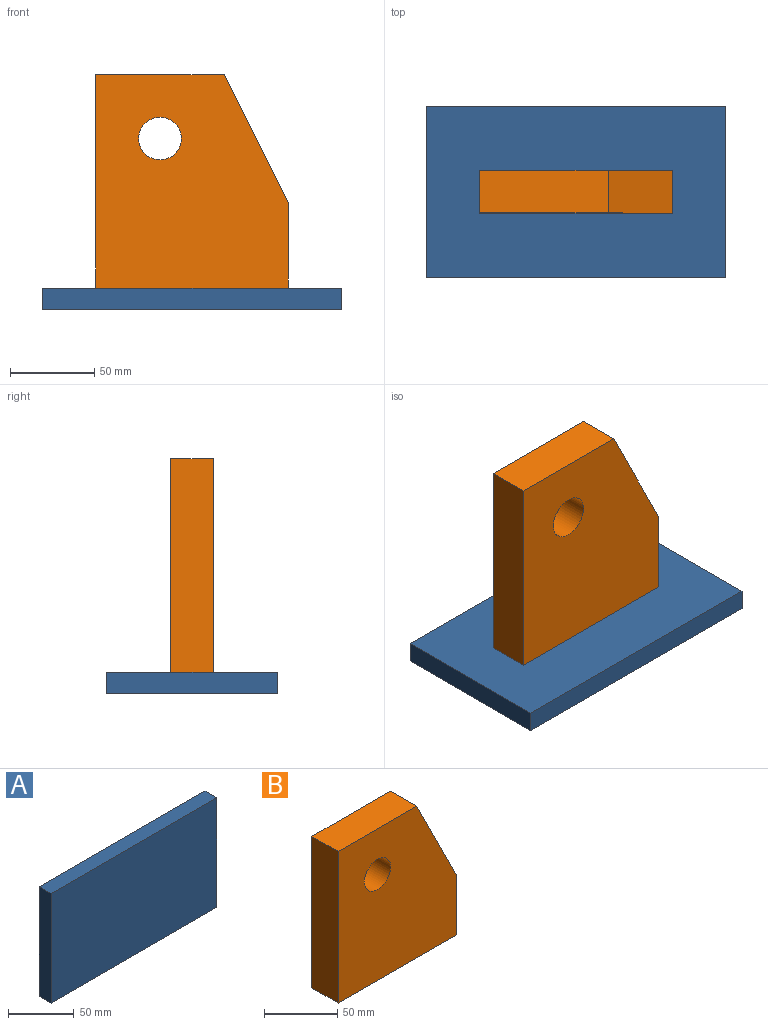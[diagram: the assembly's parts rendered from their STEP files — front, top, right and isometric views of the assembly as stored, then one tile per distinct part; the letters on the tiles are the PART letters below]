
ASSEMBLY  parts=2 mates=1
PART A: 6 faces, bbox 177.8x12.7x101.6 mm
  f0: plane 177.8x12.7mm, normal (0,0,1), area 2258.1mm2, adj f1,f3,f4,f5
  f1: plane 101.6x12.7mm, normal (-1,0,0), area 1290.3mm2, adj f0,f2,f4,f5
  f2: plane 177.8x12.7mm, normal (0,0,-1), area 2258.1mm2, adj f1,f3,f4,f5
  f3: plane 101.6x12.7mm, normal (1,0,0), area 1290.3mm2, adj f0,f2,f4,f5
  f4: plane 177.8x101.6mm, normal (0,-1,0), area 18064.5mm2, adj f0,f1,f2,f3
  f5: plane 177.8x101.6mm, normal (0,1,0), area 18064.5mm2, adj f0,f1,f2,f3
PART B: 8 faces, bbox 114.3x25.4x127 mm
  f0: plane 76.2x25.4mm, normal (0,0,1), area 1935.5mm2, adj f1,f5,f6,f7
  f1: plane 127x25.4mm, normal (-1,0,0), area 3225.8mm2, adj f0,f2,f6,f7
  f2: plane 114.3x25.4mm, normal (0,0,-1), area 2903.2mm2, adj f1,f3,f6,f7
  f3: plane 50.8x25.4mm, normal (1,0,0), area 1290.3mm2, adj f2,f5,f6,f7
  f4: cylinder r=12.7mm len=25.4mm, axis (0,1,0), area 2026.8mm2, adj f6,f7
  f5: plane 76.2x38.1mm, normal (0.89,0,0.45), area 2163.9mm2, adj f0,f3,f6,f7
  f6: plane 127x114.3mm, normal (0,-1,0), area 12557.8mm2, adj f0,f1,f2,f3,f4,f5
  f7: plane 127x114.3mm, normal (0,1,0), area 12557.8mm2, adj f0,f1,f2,f3,f4,f5
PLACE A rot(axis=(-1,0,0),90deg) t=(-93.67,-42.71,-59.14)mm
PLACE B t=(-93.67,-30.01,17.06)mm
MATE fastened A.f4 <-> B.f2  axis (0,0,1) through (-93.67,-42.71,-46.44)mm
